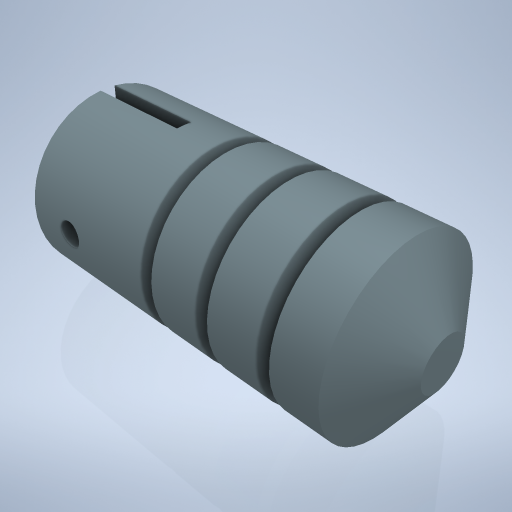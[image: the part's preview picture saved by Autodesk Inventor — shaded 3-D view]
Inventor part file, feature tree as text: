
AUTODESK INVENTOR PART (.ipt)
format: ipt  version: 2024.2 (Build 282272000, 272)  size: 298,496 bytes
history: native  units: mm
features: sketch x3, revolve x1, extrude x1, plane x1, hole x1, projected_geometry x1
ambient origin geometry x8: Origin, YZ Plane, XZ Plane, XY Plane, X Axis, Y Axis, Z Axis, Center Point
bodies: Volumenkörper1 (feature_tree)
feature tree (8):
  revolve  "Umdrehung1"
  extrude  "Extrusion1"  TaperAngle=60.0deg  [1 undecoded]
  plane  "Arbeitsebene1"
  hole  "Bohrung1"  [1 undecoded]
  sketch  "Skizze4"  dims[d7=1.0mm d8=60.0deg]
  sketch  "Skizze5"  dims[d9=4.0mm d10=14.0mm]
  projected_geometry  "Projizierte Kontur1"
  sketch  "Skizze6"  dims[d11=7.0mm d12=29.0mm d13=12.0mm d14=17.0mm d15=30.0deg d16=1.0mm d17=90.0deg d18=1.2mm d19=8.0mm d20=0.0mm d21=0.0mm d22=4.0mm d23=2.0mm d24=6.0mm d25=10.0mm d26=14.0mm d27=90.0deg d28=17.5mm d29=0.0mm]
note: 2 required parameter values undecoded (feature->parameter linkage not recoverable at this tier; creation-order binding heuristic only, values carry confidence <= 0.55)
